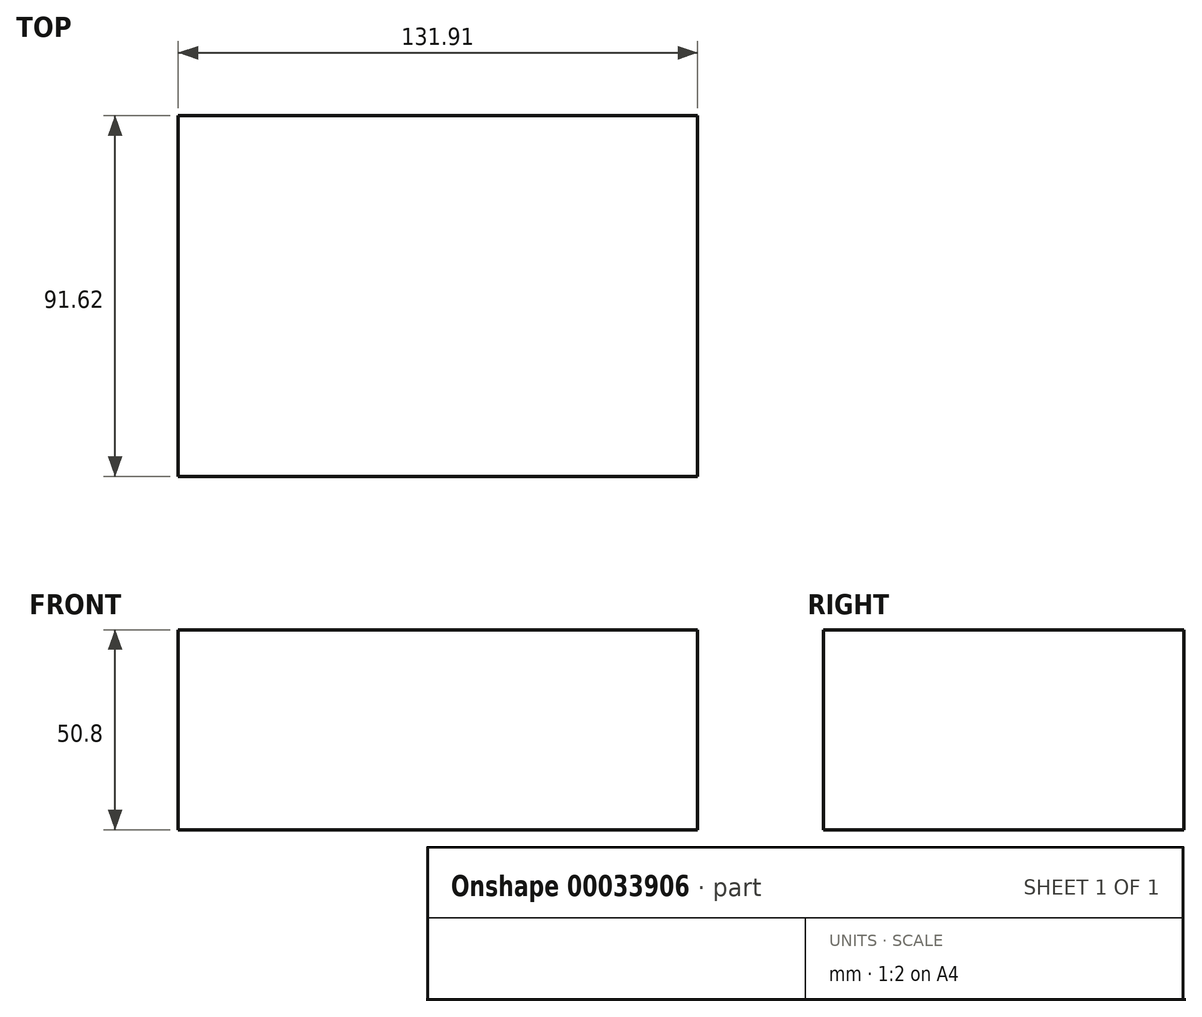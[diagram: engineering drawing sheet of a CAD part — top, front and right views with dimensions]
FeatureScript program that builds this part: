
annotation { "Feature Type Name" : "Feature", "Feature Type Description" : "" }
export const myFeature = defineFeature(function(context is Context, id is Id, definition is map)
    precondition{}
    {
        {
            var Q0;
            Q0=qCreatedBy(makeId("Top.planeOp"),FACE);
            var sketch = newSketch(context, id + "F0", { "sketchPlane" : qUnion([Q0])});
            skLineSegment(sketch, "E0", {"start": v(-75.77, 57.34) * mm, "end": v(56.14, 57.34) * mm});
            skLineSegment(sketch, "E1", {"start": v(56.14, 57.34) * mm, "end": v(56.14, -34.28) * mm});
            skLineSegment(sketch, "E2", {"start": v(56.14, -34.28) * mm, "end": v(-75.77, -34.28) * mm});
            skLineSegment(sketch, "E3", {"start": v(-75.77, -34.28) * mm, "end": v(-75.77, 57.34) * mm});
            skSolve(sketch);
        }
        {
            var Q0;
            Q0=makeQuery(id+"F0.imprint","IMPRINT",FACE,{"disambiguationData":[TD([[makeQuery(id+"F0.imprint","IMPRINT",EDGE,{"derivedFrom":sQuery(id+"F0.wireOp",EDGE,"E0")}),-1.0]])]});
            extrude(context, id + "F1", {"entities" : qUnion([Q0]), "depth" : 50.8 * mm});
        }
    });
